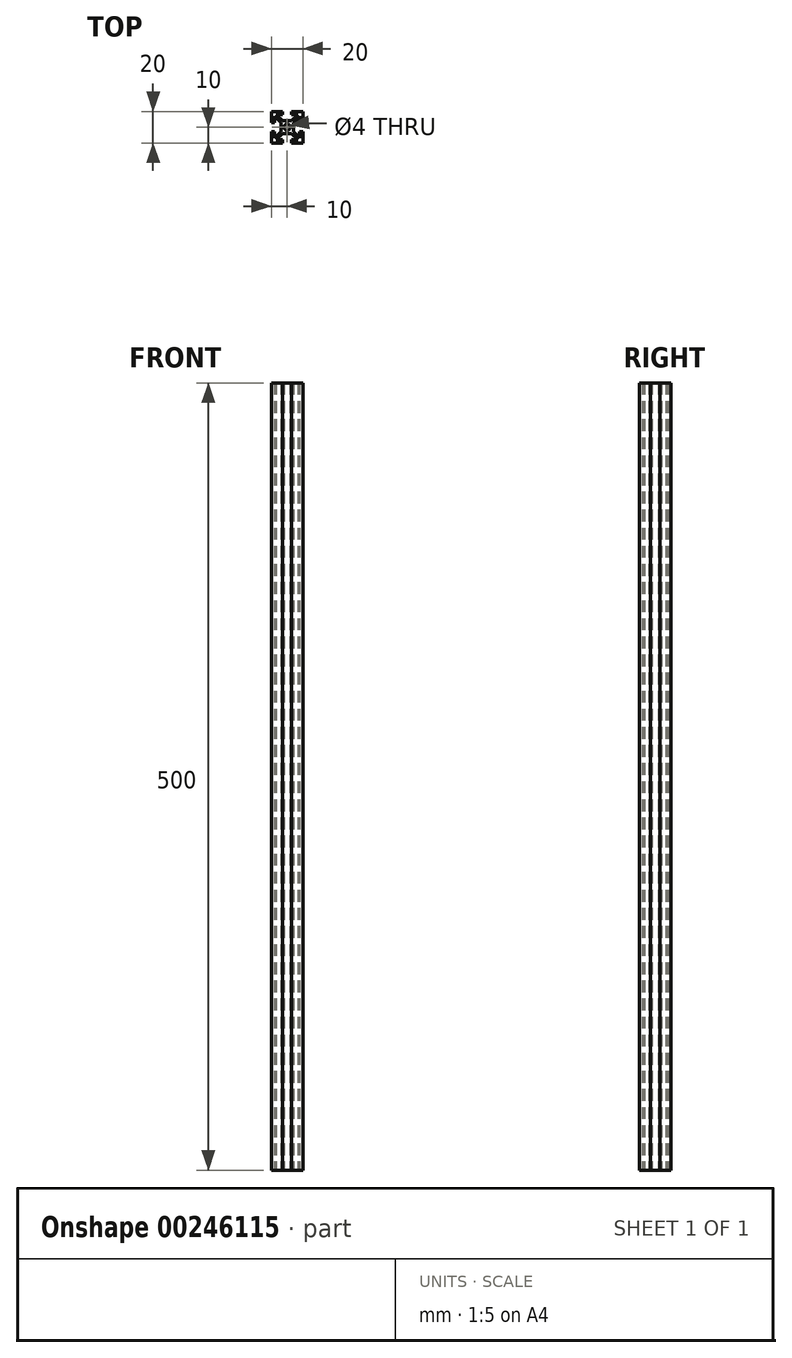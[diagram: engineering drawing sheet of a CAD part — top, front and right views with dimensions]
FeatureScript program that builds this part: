
annotation { "Feature Type Name" : "Feature", "Feature Type Description" : "" }
export const myFeature = defineFeature(function(context is Context, id is Id, definition is map)
    precondition{}
    {
        {
            var Q0;
            Q0=qCreatedBy(makeId("Top.planeOp"),FACE);
            var sketch = newSketch(context, id + "F0", { "sketchPlane" : qUnion([Q0])});
            skLineSegment(sketch, "E0.bottom", {"start": v(10, 10) * mm, "end": v(-10, 10) * mm, "construction": true});
            skLineSegment(sketch, "E0.top", {"start": v(10, -10) * mm, "end": v(-10, -10) * mm, "construction": true});
            skLineSegment(sketch, "E0.left", {"start": v(10, 10) * mm, "end": v(10, -10) * mm, "construction": true});
            skLineSegment(sketch, "E0.right", {"start": v(-10, 10) * mm, "end": v(-10, -10) * mm, "construction": true});
            skPoint(sketch, "E0.middle", {"position": v(0, 0) * mm});
            skLineSegment(sketch, "E1", {"start": v(0, 4) * mm, "end": v(-2.94, 4) * mm});
            skLineSegment(sketch, "E2", {"start": v(-2.94, 4) * mm, "end": v(-6.94, 8) * mm});
            skLineSegment(sketch, "E3", {"start": v(-6.94, 8) * mm, "end": v(-2.94, 8) * mm});
            skLineSegment(sketch, "E4", {"start": v(-10, 10) * mm, "end": v(10, -10) * mm, "construction": true});
            skArc(sketch, "E5", {"start": v(0, 2) * mm, "mid": v(-0.77, 1.85) * mm, "end": v(-1.41, 1.41) * mm});
            skLineSegment(sketch, "E6", {"start": v(-2.94, 8) * mm, "end": v(-2.94, 10) * mm});
            skLineSegment(sketch, "E7", {"start": v(-2.94, 10) * mm, "end": v(-10, 10) * mm});
            skLineSegment(sketch, "E8.MirrorCS", {"start": v(-10, 2.94) * mm, "end": v(-10, 10) * mm});
            skLineSegment(sketch, "E9.MirrorCS", {"start": v(-8, 2.94) * mm, "end": v(-10, 2.94) * mm});
            skLineSegment(sketch, "E10.MirrorCS", {"start": v(-8, 6.94) * mm, "end": v(-8, 2.94) * mm});
            skLineSegment(sketch, "E11.MirrorCS", {"start": v(-4, 2.94) * mm, "end": v(-8, 6.94) * mm});
            skLineSegment(sketch, "E12.MirrorCS", {"start": v(-4, 0) * mm, "end": v(-4, 2.94) * mm});
            skArc(sketch, "E13.MirrorCS", {"start": v(-2, 0) * mm, "mid": v(-1.85, 0.77) * mm, "end": v(-1.41, 1.41) * mm});
            skLineSegment(sketch, "E14.MirrorCS", {"start": v(-4, 0) * mm, "end": v(-4, -2.94) * mm});
            skLineSegment(sketch, "E15.MirrorCS", {"start": v(-4, -2.94) * mm, "end": v(-8, -6.94) * mm});
            skArc(sketch, "E16.MirrorCS", {"start": v(-2, 0) * mm, "mid": v(-1.85, -0.77) * mm, "end": v(-1.41, -1.41) * mm});
            skLineSegment(sketch, "E17.MirrorCS", {"start": v(-8, -6.94) * mm, "end": v(-8, -2.94) * mm});
            skLineSegment(sketch, "E18.MirrorCS", {"start": v(-6.94, -8) * mm, "end": v(-2.94, -8) * mm});
            skLineSegment(sketch, "E19.MirrorCS", {"start": v(-2.94, -10) * mm, "end": v(-10, -10) * mm});
            skLineSegment(sketch, "E20.MirrorCS", {"start": v(-2.94, -4) * mm, "end": v(-6.94, -8) * mm});
            skArc(sketch, "E21.MirrorCS", {"start": v(0, -2) * mm, "mid": v(-0.77, -1.85) * mm, "end": v(-1.41, -1.41) * mm});
            skLineSegment(sketch, "E22.MirrorCS", {"start": v(0, -4) * mm, "end": v(-2.94, -4) * mm});
            skLineSegment(sketch, "E23.MirrorCS", {"start": v(-10, -2.94) * mm, "end": v(-10, -10) * mm});
            skLineSegment(sketch, "E24.MirrorCS", {"start": v(-2.94, -8) * mm, "end": v(-2.94, -10) * mm});
            skLineSegment(sketch, "E25.MirrorCS", {"start": v(-8, -2.94) * mm, "end": v(-10, -2.94) * mm});
            skLineSegment(sketch, "E26.MirrorCS", {"start": v(10, -2.94) * mm, "end": v(10, -10) * mm});
            skLineSegment(sketch, "E27.MirrorCS", {"start": v(8, -2.94) * mm, "end": v(10, -2.94) * mm});
            skArc(sketch, "E28.MirrorCS", {"start": v(2, 0) * mm, "mid": v(1.85, -0.77) * mm, "end": v(1.41, -1.41) * mm});
            skArc(sketch, "E29.MirrorCS", {"start": v(0, -2) * mm, "mid": v(0.77, -1.85) * mm, "end": v(1.41, -1.41) * mm});
            skLineSegment(sketch, "E30.MirrorCS", {"start": v(8, 6.94) * mm, "end": v(8, 2.94) * mm});
            skLineSegment(sketch, "E31.MirrorCS", {"start": v(6.94, -8) * mm, "end": v(2.94, -8) * mm});
            skLineSegment(sketch, "E32.MirrorCS", {"start": v(4, 2.94) * mm, "end": v(8, 6.94) * mm});
            skLineSegment(sketch, "E33.MirrorCS", {"start": v(4, 0) * mm, "end": v(4, 2.94) * mm});
            skLineSegment(sketch, "E34.MirrorCS", {"start": v(4, 0) * mm, "end": v(4, -2.94) * mm});
            skLineSegment(sketch, "E35.MirrorCS", {"start": v(0, -4) * mm, "end": v(2.94, -4) * mm});
            skLineSegment(sketch, "E36.MirrorCS", {"start": v(2.94, -10) * mm, "end": v(10, -10) * mm});
            skLineSegment(sketch, "E37.MirrorCS", {"start": v(4, -2.94) * mm, "end": v(8, -6.94) * mm});
            skLineSegment(sketch, "E38.MirrorCS", {"start": v(0, 4) * mm, "end": v(2.94, 4) * mm});
            skLineSegment(sketch, "E39.MirrorCS", {"start": v(2.94, 4) * mm, "end": v(6.94, 8) * mm});
            skLineSegment(sketch, "E40.MirrorCS", {"start": v(6.94, 8) * mm, "end": v(2.94, 8) * mm});
            skArc(sketch, "E41.MirrorCS", {"start": v(2, 0) * mm, "mid": v(1.85, 0.77) * mm, "end": v(1.41, 1.41) * mm});
            skLineSegment(sketch, "E42.MirrorCS", {"start": v(8, -6.94) * mm, "end": v(8, -2.94) * mm});
            skLineSegment(sketch, "E43.MirrorCS", {"start": v(2.94, -4) * mm, "end": v(6.94, -8) * mm});
            skLineSegment(sketch, "E44.MirrorCS", {"start": v(2.94, -8) * mm, "end": v(2.94, -10) * mm});
            skLineSegment(sketch, "E45.MirrorCS", {"start": v(2.94, 8) * mm, "end": v(2.94, 10) * mm});
            skLineSegment(sketch, "E46.MirrorCS", {"start": v(2.94, 10) * mm, "end": v(10, 10) * mm});
            skArc(sketch, "E47.MirrorCS", {"start": v(0, 2) * mm, "mid": v(0.77, 1.85) * mm, "end": v(1.41, 1.41) * mm});
            skLineSegment(sketch, "E48.MirrorCS", {"start": v(10, 2.94) * mm, "end": v(10, 10) * mm});
            skLineSegment(sketch, "E49.MirrorCS", {"start": v(8, 2.94) * mm, "end": v(10, 2.94) * mm});
            skSolve(sketch);
        }
        {
            var Q0;
            Q0 = qSketchRegion(id + "F0", true);
            extrude(context, id + "F1", {"entities" : qUnion([Q0]), "flatOperationType" : FlatOperationType.REMOVE, "thickness1" : 5 * mm, "thickness2" : 0 * mm, "thickness" : 5 * mm, "offsetDistance" : 25 * mm, "startOffsetBound" : StartOffsetType.BLIND, "startOffsetDistance" : 25 * mm, "depth" : 500 * mm, "symmetric" : true, "domain" : OperationDomain.MODEL});
        }
    });
